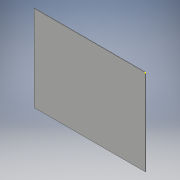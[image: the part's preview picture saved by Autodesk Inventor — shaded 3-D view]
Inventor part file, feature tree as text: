
AUTODESK INVENTOR PART (.ipt)
format: ipt  version: 2017 (Build 210142000, 142)  size: 87,040 bytes
history: native  units: mm
features: sketch x2, extrude x1
ambient origin geometry x8: Origin, YZ Plane, XZ Plane, XY Plane, X Axis, Y Axis, Z Axis, Center Point
bodies: Solid1 (feature_tree)
feature tree (3):
  sketch  "Sketch1"  dims[d0=215.9mm d1=279.4mm]
  extrude  "Extrusion1"  Depth=279.4mm
  sketch  "Sketch2"  dims[d2=1.0mm d3=0.0mm]
